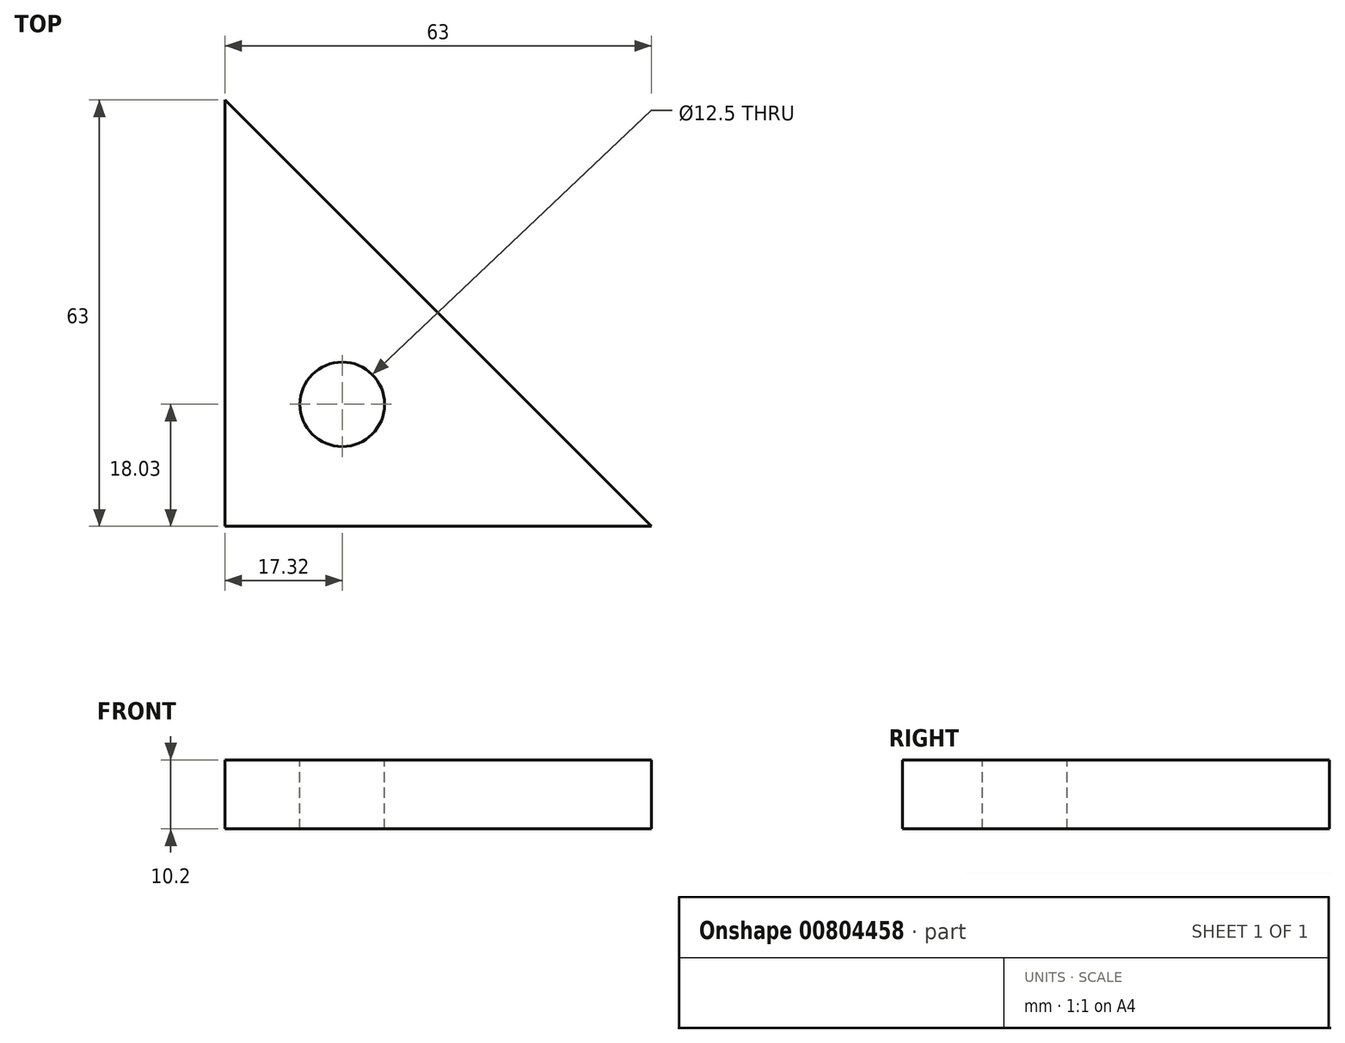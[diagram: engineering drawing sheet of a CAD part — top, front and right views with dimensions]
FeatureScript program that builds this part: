
annotation { "Feature Type Name" : "Feature", "Feature Type Description" : "" }
export const myFeature = defineFeature(function(context is Context, id is Id, definition is map)
    precondition{}
    {
        {
            var Q0;
            Q0=qCreatedBy(makeId("Top.planeOp"),FACE);
            var sketch = newSketch(context, id + "F0", { "sketchPlane" : qUnion([Q0])});
            skLineSegment(sketch, "E0", {"start": v(-17.32, -18.03) * mm, "end": v(45.68, -18.03) * mm});
            skLineSegment(sketch, "E1", {"start": v(-17.32, -18.03) * mm, "end": v(-17.32, 44.97) * mm});
            skLineSegment(sketch, "E2", {"start": v(-17.32, 44.97) * mm, "end": v(45.68, -18.03) * mm});
            skSolve(sketch);
        }
        {
            var Q0;
            Q0=qSketchRegion(id+"F0",true);
            extrude(context, id + "F1", {"entities" : qUnion([Q0]), "depth" : 10.2 * mm, "offsetDistance" : 25.4 * mm});
        }
        {
            var Q0;
            Q0=makeQuery(id+"F1.opExtrude","CAP_FACE",FACE,{"disambiguationData":[OSD([sQuery(id+"F0.wireOp",EDGE,"E0"),sQuery(id+"F0.wireOp",EDGE,"E1"),sQuery(id+"F0.wireOp",EDGE,"E2")])],"isStart":false});
            var sketch = newSketch(context, id + "F2", { "sketchPlane" : qUnion([Q0])});
            skCircle(sketch, "E3", {"center": v(0, 0) * mm, "radius": 6.25 * mm});
            skSolve(sketch);
        }
        {
            var Q0;
            Q0=qSketchRegion(id+"F2",true);
            extrude(context, id + "F3", {"entities" : qUnion([Q0]), "operationType" : NewBodyOperationType.REMOVE, "endBound" : BoundingType.THROUGH_ALL, "oppositeDirection" : true, "depth" : 2 * mm, "offsetDistance" : 25.4 * mm});
        }
    });
